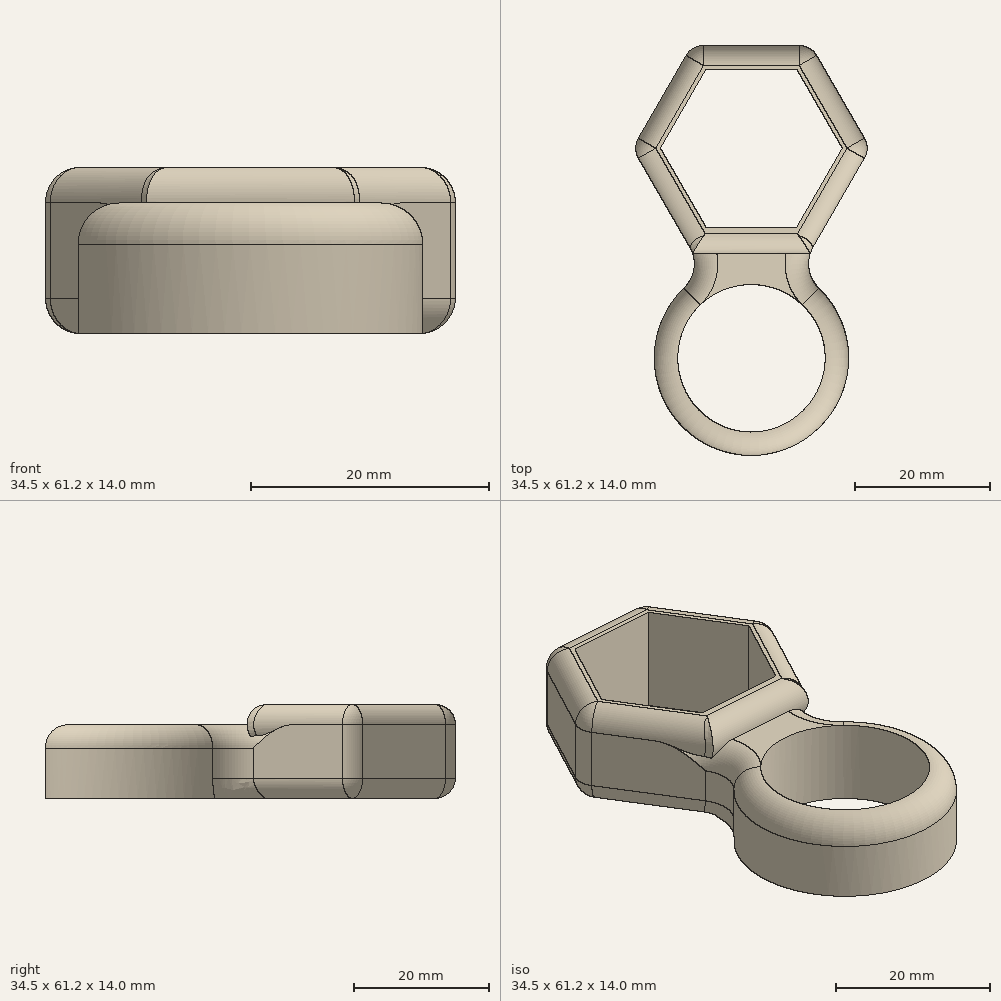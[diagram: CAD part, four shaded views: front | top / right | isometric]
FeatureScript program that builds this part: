
annotation { "Feature Type Name" : "Feature", "Feature Type Description" : "" }
export const myFeature = defineFeature(function(context is Context, id is Id, definition is map)
    precondition{}
    {
        {
            var Q0;
            Q0=qCreatedBy(makeId("Top.planeOp"),FACE);
            var sketch = newSketch(context, id + "F0", { "sketchPlane" : qUnion([Q0])});
            skCircle(sketch, "E0", {"center": v(0, 0) * mm, "radius": 47.5 * mm, "construction": true});
            skLineSegment(sketch, "E1", {"start": v(0, 32) * mm, "end": v(0, 0) * mm, "construction": true});
            skLineSegment(sketch, "E2", {"start": v(0, 0) * mm, "end": v(-27.71, -16) * mm, "construction": true});
            skLineSegment(sketch, "E3", {"start": v(0, 0) * mm, "end": v(27.71, -16) * mm, "construction": true});
            skCircle(sketch, "E4", {"center": v(0, 0) * mm, "radius": 14.5 * mm});
            skCircle(sketch, "E5.cCircle", {"center": v(0, 31.32) * mm, "radius": 11.75 * mm, "construction": true});
            skLineSegment(sketch, "E5.0", {"start": v(13.57, 31.32) * mm, "end": v(6.78, 19.57) * mm});
            skLineSegment(sketch, "E5.1", {"start": v(6.78, 19.57) * mm, "end": v(-6.78, 19.57) * mm});
            skLineSegment(sketch, "E5.2", {"start": v(-6.78, 19.57) * mm, "end": v(-13.57, 31.32) * mm});
            skLineSegment(sketch, "E5.3", {"start": v(-13.57, 31.32) * mm, "end": v(-6.78, 43.07) * mm});
            skLineSegment(sketch, "E5.4", {"start": v(-6.78, 43.07) * mm, "end": v(6.78, 43.07) * mm});
            skLineSegment(sketch, "E5.5", {"start": v(6.78, 43.07) * mm, "end": v(13.57, 31.32) * mm});
            skPoint(sketch, "E5.0.midPoint", {"position": v(10.18, 25.44) * mm});
            skCircle(sketch, "E6.cCircle", {"center": v(0, 31.32) * mm, "radius": 15.35 * mm, "construction": true});
            skLineSegment(sketch, "E6.0", {"start": v(17.72, 31.32) * mm, "end": v(8.86, 15.97) * mm});
            skLineSegment(sketch, "E6.1", {"start": v(8.86, 15.97) * mm, "end": v(-8.86, 15.97) * mm});
            skLineSegment(sketch, "E6.2", {"start": v(-8.86, 15.97) * mm, "end": v(-17.72, 31.32) * mm});
            skLineSegment(sketch, "E6.3", {"start": v(-17.72, 31.32) * mm, "end": v(-8.86, 46.67) * mm});
            skLineSegment(sketch, "E6.4", {"start": v(-8.86, 46.67) * mm, "end": v(8.86, 46.67) * mm});
            skLineSegment(sketch, "E6.5", {"start": v(8.86, 46.67) * mm, "end": v(17.72, 31.32) * mm});
            skPoint(sketch, "E6.0.midPoint", {"position": v(13.3, 23.64) * mm});
            skLineSegment(sketch, "E7", {"start": v(-8.86, 15.97) * mm, "end": v(-6.98, 12.7) * mm});
            skLineSegment(sketch, "E8", {"start": v(8.86, 15.97) * mm, "end": v(6.98, 12.7) * mm});
            skSolve(sketch);
        }
        {
            var Q0;
            Q0=qCreatedBy(makeId("Top.planeOp"),FACE);
            var sketch = newSketch(context, id + "F1", { "sketchPlane" : qUnion([Q0])});
            skCircle(sketch, "E9", {"center": v(0, 0) * mm, "radius": 11 * mm});
            skSolve(sketch);
        }
        {
            var Q0;
            Q0=qSketchRegion(id+"F0",true);
            extrude(context, id + "F2", {"entities" : qUnion([Q0]), "endBound" : BoundingType.SYMMETRIC, "depth" : 14 * mm, "offsetDistance" : 25 * mm});
        }
        {
            var Q0;
            Q0=makeQuery(id+"F2.opExtrude","CAP_FACE",FACE,{"disambiguationData":[OSD([sQuery(id+"F0.wireOp",EDGE,"E4"),sQuery(id+"F0.wireOp",EDGE,"E5.0"),sQuery(id+"F0.wireOp",EDGE,"E5.1"),sQuery(id+"F0.wireOp",EDGE,"E5.2"),sQuery(id+"F0.wireOp",EDGE,"E5.3"),sQuery(id+"F0.wireOp",EDGE,"E5.4"),sQuery(id+"F0.wireOp",EDGE,"E5.5"),sQuery(id+"F0.wireOp",EDGE,"E6.0"),sQuery(id+"F0.wireOp",EDGE,"E6.2"),sQuery(id+"F0.wireOp",EDGE,"E6.3"),sQuery(id+"F0.wireOp",EDGE,"E6.4"),sQuery(id+"F0.wireOp",EDGE,"E6.5"),sQuery(id+"F0.wireOp",EDGE,"E7"),sQuery(id+"F0.wireOp",EDGE,"E8")])],"isStart":false});
            var sketch = newSketch(context, id + "F3", { "sketchPlane" : qUnion([Q0])});
            skCircle(sketch, "E10", {"center": v(9.7, -5.3) * mm, "radius": 1.46 * mm});
            skSolve(sketch);
        }
        {
            var Q0;
            Q0=qSketchRegion(id+"F3",true);
            extrude(context, id + "F4", {"entities" : qUnion([Q0]), "operationType" : NewBodyOperationType.ADD, "oppositeDirection" : true, "depth" : 1 * mm, "offsetDistance" : 25 * mm});
        }
        {
            var Q0;
            Q0=qSketchRegion(id+"F1",true);
            extrude(context, id + "F5", {"entities" : qUnion([Q0]), "operationType" : NewBodyOperationType.REMOVE, "endBound" : BoundingType.SYMMETRIC, "oppositeDirection" : true, "depth" : 25 * mm, "offsetDistance" : 25 * mm});
        }
        {
            var Q0;
            Q0=qCreatedBy(makeId("Top.planeOp"),FACE);
            cPlane(context, id + "F6", {"entities" : qUnion([Q0]), "cplaneType" : CPlaneType.OFFSET, "offset" : 4 * mm, "width" : 150 * mm, "height" : 150 * mm});
        }
        {
            var Q0;
            Q0=qCreatedBy(id+"F6.planeOp",FACE);
            var sketch = newSketch(context, id + "F7", { "sketchPlane" : qUnion([Q0])});
            skCircle(sketch, "E11.cCircle", {"center": v(0, 0) * mm, "radius": 15.57 * mm, "construction": true});
            skLineSegment(sketch, "E11.0", {"start": v(8.99, 15.57) * mm, "end": v(17.97, 0) * mm});
            skLineSegment(sketch, "E11.1", {"start": v(17.97, 0) * mm, "end": v(8.99, -15.57) * mm});
            skLineSegment(sketch, "E11.2", {"start": v(8.99, -15.57) * mm, "end": v(-8.99, -15.57) * mm});
            skLineSegment(sketch, "E11.3", {"start": v(-8.99, -15.57) * mm, "end": v(-17.97, 0) * mm});
            skLineSegment(sketch, "E11.4", {"start": v(-17.97, 0) * mm, "end": v(-8.99, 15.57) * mm});
            skLineSegment(sketch, "E11.5", {"start": v(-8.99, 15.57) * mm, "end": v(8.99, 15.57) * mm});
            skPoint(sketch, "E11.0.midPoint", {"position": v(13.48, 7.78) * mm});
            skSolve(sketch);
        }
        {
            var Q0;
            Q0=qSketchRegion(id+"F7",true);
            extrude(context, id + "F8", {"entities" : qUnion([Q0]), "operationType" : NewBodyOperationType.REMOVE, "depth" : 3.5 * mm, "offsetDistance" : 25 * mm});
        }
        {
            var Q0;
            Q0=makeQuery(id+"FCyTIovh0KCK1Vn_1.2.F2.opExtrude","SWEPT_FACE",FACE,{"disambiguationData":[OSD([sQuery(id+"F0.wireOp",EDGE,"E6.4")])]});
            var Q1;
            Q1=makeQuery(id+"FCyTIovh0KCK1Vn_1.2.F2.opExtrude","SWEPT_FACE",FACE,{"disambiguationData":[OSD([sQuery(id+"F0.wireOp",EDGE,"E6.3")])]});
            var Q2;
            Q2=makeQuery(id+"FCyTIovh0KCK1Vn_1.2.F2.opExtrude","SWEPT_FACE",FACE,{"disambiguationData":[OSD([sQuery(id+"F0.wireOp",EDGE,"E6.5")])]});
            var Q3;
            Q3=makeQuery(id+"F2.opExtrude","SWEPT_FACE",FACE,{"disambiguationData":[OSD([sQuery(id+"F0.wireOp",EDGE,"E6.5")])]});
            var Q4;
            Q4=makeQuery(id+"F2.opExtrude","SWEPT_FACE",FACE,{"disambiguationData":[OSD([sQuery(id+"F0.wireOp",EDGE,"E6.3")])]});
            var Q5;
            Q5=makeQuery(id+"F2.opExtrude","SWEPT_FACE",FACE,{"disambiguationData":[OSD([sQuery(id+"F0.wireOp",EDGE,"E6.4")])]});
            var Q6;
            Q6=makeQuery(id+"FCyTIovh0KCK1Vn_1.1.F2.opExtrude","SWEPT_FACE",FACE,{"disambiguationData":[OSD([sQuery(id+"F0.wireOp",EDGE,"E6.5")])]});
            var Q7;
            Q7=makeQuery(id+"FCyTIovh0KCK1Vn_1.1.F2.opExtrude","SWEPT_FACE",FACE,{"disambiguationData":[OSD([sQuery(id+"F0.wireOp",EDGE,"E6.4")])]});
            var Q8;
            Q8=makeQuery(id+"FCyTIovh0KCK1Vn_1.1.F2.opExtrude","SWEPT_FACE",FACE,{"disambiguationData":[OSD([sQuery(id+"F0.wireOp",EDGE,"E6.3")])]});
            var Q9;
            Q9=makeQuery(id+"FCyTIovh0KCK1Vn_1.1.F2.opExtrude","CAP_EDGE",EDGE,{"disambiguationData":[OSD([sQuery(id+"F0.wireOp",EDGE,"E6.2"),sQuery(id+"F0.wireOp",EDGE,"E7")])],"isStart":true});
            var Q10;
            Q10=makeQuery(id+"FCyTIovh0KCK1Vn_1.1.F2.opExtrude","CAP_EDGE",EDGE,{"disambiguationData":[OSD([sQuery(id+"F0.wireOp",EDGE,"E6.2"),sQuery(id+"F0.wireOp",EDGE,"E7")])],"isStart":false});
            var Q11;
            {var subQ0=sQuery(id+"F0.wireOp",EDGE,"E8");var subQ1=sQuery(id+"F0.wireOp",EDGE,"E7");var subQ2=sQuery(id+"F0.wireOp",EDGE,"E6.5");var subQ3=sQuery(id+"F0.wireOp",EDGE,"E6.4");var subQ4=sQuery(id+"F0.wireOp",EDGE,"E6.3");var subQ5=sQuery(id+"F0.wireOp",EDGE,"E6.2");var subQ6=sQuery(id+"F0.wireOp",EDGE,"E6.0");var subQ7=sQuery(id+"F0.wireOp",EDGE,"E5.5");var subQ8=sQuery(id+"F0.wireOp",EDGE,"E5.4");var subQ9=sQuery(id+"F0.wireOp",EDGE,"E5.3");var subQ10=sQuery(id+"F0.wireOp",EDGE,"E5.2");var subQ11=sQuery(id+"F0.wireOp",EDGE,"E5.1");var subQ12=sQuery(id+"F0.wireOp",EDGE,"E5.0");var subQ13=sQuery(id+"F0.wireOp",EDGE,"E4");Q11=makeQuery(id+"F8.boolean.opBoolean","INTERSECT",EDGE,{"derivedFrom":[makeQuery(id+"F4.boolean.opBoolean","MERGE",FACE,{"derivedFrom":[makeQuery(id+"F2.opExtrude","CAP_FACE",FACE,{"disambiguationData":[OSD([subQ13,subQ12,subQ11,subQ10,subQ9,subQ8,subQ7,subQ6,subQ5,subQ4,subQ3,subQ2,subQ1,subQ0])],"isStart":false}),makeQuery(id+"FCyTIovh0KCK1Vn_1.1.F2.opExtrude","CAP_FACE",FACE,{"disambiguationData":[OSD([subQ13,subQ12,subQ11,subQ10,subQ9,subQ8,subQ7,subQ6,subQ5,subQ4,subQ3,subQ2,subQ1,subQ0])],"isStart":false}),makeQuery(id+"FCyTIovh0KCK1Vn_1.2.F2.opExtrude","CAP_FACE",FACE,{"disambiguationData":[OSD([subQ13,subQ12,subQ11,subQ10,subQ9,subQ8,subQ7,subQ6,subQ5,subQ4,subQ3,subQ2,subQ1,subQ0])],"isStart":false})]}),makeQuery(id+"F8.opExtrude","SWEPT_FACE",FACE,{"disambiguationData":[OSD([sQuery(id+"F7.wireOp",EDGE,"E11.3")])]})]});}
            var Q12;
            Q12=makeQuery(id+"FCyTIovh0KCK1Vn_1.1.F2.opExtrude","CAP_EDGE",EDGE,{"disambiguationData":[OSD([sQuery(id+"F0.wireOp",EDGE,"E6.0"),sQuery(id+"F0.wireOp",EDGE,"E8")])],"isStart":false});
            var Q13;
            Q13=makeQuery(id+"FCyTIovh0KCK1Vn_1.1.F2.opExtrude","CAP_EDGE",EDGE,{"disambiguationData":[OSD([sQuery(id+"F0.wireOp",EDGE,"E6.0"),sQuery(id+"F0.wireOp",EDGE,"E8")])],"isStart":true});
            var Q14;
            {var subQ0=sQuery(id+"F0.wireOp",EDGE,"E8");var subQ1=sQuery(id+"F0.wireOp",EDGE,"E7");var subQ2=sQuery(id+"F0.wireOp",EDGE,"E6.5");var subQ3=sQuery(id+"F0.wireOp",EDGE,"E6.4");var subQ4=sQuery(id+"F0.wireOp",EDGE,"E6.3");var subQ5=sQuery(id+"F0.wireOp",EDGE,"E6.2");var subQ6=sQuery(id+"F0.wireOp",EDGE,"E6.0");var subQ7=sQuery(id+"F0.wireOp",EDGE,"E5.5");var subQ8=sQuery(id+"F0.wireOp",EDGE,"E5.4");var subQ9=sQuery(id+"F0.wireOp",EDGE,"E5.3");var subQ10=sQuery(id+"F0.wireOp",EDGE,"E5.2");var subQ11=sQuery(id+"F0.wireOp",EDGE,"E5.1");var subQ12=sQuery(id+"F0.wireOp",EDGE,"E5.0");var subQ13=sQuery(id+"F0.wireOp",EDGE,"E4");Q14=makeQuery(id+"Fe9b3TNG2FXQlZz_1.1.F8.boolean.opBoolean","INTERSECT",EDGE,{"derivedFrom":[makeQuery(id+"F4.boolean.opBoolean","MERGE",FACE,{"derivedFrom":[makeQuery(id+"F2.opExtrude","CAP_FACE",FACE,{"disambiguationData":[OSD([subQ13,subQ12,subQ11,subQ10,subQ9,subQ8,subQ7,subQ6,subQ5,subQ4,subQ3,subQ2,subQ1,subQ0])],"isStart":true}),makeQuery(id+"FCyTIovh0KCK1Vn_1.1.F2.opExtrude","CAP_FACE",FACE,{"disambiguationData":[OSD([subQ13,subQ12,subQ11,subQ10,subQ9,subQ8,subQ7,subQ6,subQ5,subQ4,subQ3,subQ2,subQ1,subQ0])],"isStart":true}),makeQuery(id+"FCyTIovh0KCK1Vn_1.2.F2.opExtrude","CAP_FACE",FACE,{"disambiguationData":[OSD([subQ13,subQ12,subQ11,subQ10,subQ9,subQ8,subQ7,subQ6,subQ5,subQ4,subQ3,subQ2,subQ1,subQ0])],"isStart":true})]}),makeQuery(id+"Fe9b3TNG2FXQlZz_1.1.F8.opExtrude","SWEPT_FACE",FACE,{"disambiguationData":[OSD([sQuery(id+"F7.wireOp",EDGE,"E11.3")])]})]});}
            var Q15;
            Q15=makeQuery(id+"FCyTIovh0KCK1Vn_1.2.F2.opExtrude","CAP_EDGE",EDGE,{"disambiguationData":[OSD([sQuery(id+"F0.wireOp",EDGE,"E6.0"),sQuery(id+"F0.wireOp",EDGE,"E8")])],"isStart":true});
            var Q16;
            {var subQ0=sQuery(id+"F0.wireOp",EDGE,"E8");var subQ1=sQuery(id+"F0.wireOp",EDGE,"E7");var subQ2=sQuery(id+"F0.wireOp",EDGE,"E6.5");var subQ3=sQuery(id+"F0.wireOp",EDGE,"E6.4");var subQ4=sQuery(id+"F0.wireOp",EDGE,"E6.3");var subQ5=sQuery(id+"F0.wireOp",EDGE,"E6.2");var subQ6=sQuery(id+"F0.wireOp",EDGE,"E6.0");var subQ7=sQuery(id+"F0.wireOp",EDGE,"E5.5");var subQ8=sQuery(id+"F0.wireOp",EDGE,"E5.4");var subQ9=sQuery(id+"F0.wireOp",EDGE,"E5.3");var subQ10=sQuery(id+"F0.wireOp",EDGE,"E5.2");var subQ11=sQuery(id+"F0.wireOp",EDGE,"E5.1");var subQ12=sQuery(id+"F0.wireOp",EDGE,"E5.0");var subQ13=sQuery(id+"F0.wireOp",EDGE,"E4");Q16=makeQuery(id+"Fe9b3TNG2FXQlZz_1.1.F8.boolean.opBoolean","INTERSECT",EDGE,{"derivedFrom":[makeQuery(id+"F4.boolean.opBoolean","MERGE",FACE,{"derivedFrom":[makeQuery(id+"F2.opExtrude","CAP_FACE",FACE,{"disambiguationData":[OSD([subQ13,subQ12,subQ11,subQ10,subQ9,subQ8,subQ7,subQ6,subQ5,subQ4,subQ3,subQ2,subQ1,subQ0])],"isStart":true}),makeQuery(id+"FCyTIovh0KCK1Vn_1.1.F2.opExtrude","CAP_FACE",FACE,{"disambiguationData":[OSD([subQ13,subQ12,subQ11,subQ10,subQ9,subQ8,subQ7,subQ6,subQ5,subQ4,subQ3,subQ2,subQ1,subQ0])],"isStart":true}),makeQuery(id+"FCyTIovh0KCK1Vn_1.2.F2.opExtrude","CAP_FACE",FACE,{"disambiguationData":[OSD([subQ13,subQ12,subQ11,subQ10,subQ9,subQ8,subQ7,subQ6,subQ5,subQ4,subQ3,subQ2,subQ1,subQ0])],"isStart":true})]}),makeQuery(id+"Fe9b3TNG2FXQlZz_1.1.F8.opExtrude","SWEPT_FACE",FACE,{"disambiguationData":[OSD([sQuery(id+"F7.wireOp",EDGE,"E11.5")])]})]});}
            var Q17;
            Q17=makeQuery(id+"F2.opExtrude","CAP_EDGE",EDGE,{"disambiguationData":[OSD([sQuery(id+"F0.wireOp",EDGE,"E6.0"),sQuery(id+"F0.wireOp",EDGE,"E8")])],"isStart":true});
            var Q18;
            Q18=makeQuery(id+"F2.opExtrude","CAP_EDGE",EDGE,{"disambiguationData":[OSD([sQuery(id+"F0.wireOp",EDGE,"E6.2"),sQuery(id+"F0.wireOp",EDGE,"E7")])],"isStart":true});
            var Q19;
            {var subQ0=sQuery(id+"F0.wireOp",EDGE,"E8");var subQ1=sQuery(id+"F0.wireOp",EDGE,"E7");var subQ2=sQuery(id+"F0.wireOp",EDGE,"E6.5");var subQ3=sQuery(id+"F0.wireOp",EDGE,"E6.4");var subQ4=sQuery(id+"F0.wireOp",EDGE,"E6.3");var subQ5=sQuery(id+"F0.wireOp",EDGE,"E6.2");var subQ6=sQuery(id+"F0.wireOp",EDGE,"E6.0");var subQ7=sQuery(id+"F0.wireOp",EDGE,"E5.5");var subQ8=sQuery(id+"F0.wireOp",EDGE,"E5.4");var subQ9=sQuery(id+"F0.wireOp",EDGE,"E5.3");var subQ10=sQuery(id+"F0.wireOp",EDGE,"E5.2");var subQ11=sQuery(id+"F0.wireOp",EDGE,"E5.1");var subQ12=sQuery(id+"F0.wireOp",EDGE,"E5.0");var subQ13=sQuery(id+"F0.wireOp",EDGE,"E4");Q19=makeQuery(id+"Fe9b3TNG2FXQlZz_1.1.F8.boolean.opBoolean","INTERSECT",EDGE,{"derivedFrom":[makeQuery(id+"F4.boolean.opBoolean","MERGE",FACE,{"derivedFrom":[makeQuery(id+"F2.opExtrude","CAP_FACE",FACE,{"disambiguationData":[OSD([subQ13,subQ12,subQ11,subQ10,subQ9,subQ8,subQ7,subQ6,subQ5,subQ4,subQ3,subQ2,subQ1,subQ0])],"isStart":true}),makeQuery(id+"FCyTIovh0KCK1Vn_1.1.F2.opExtrude","CAP_FACE",FACE,{"disambiguationData":[OSD([subQ13,subQ12,subQ11,subQ10,subQ9,subQ8,subQ7,subQ6,subQ5,subQ4,subQ3,subQ2,subQ1,subQ0])],"isStart":true}),makeQuery(id+"FCyTIovh0KCK1Vn_1.2.F2.opExtrude","CAP_FACE",FACE,{"disambiguationData":[OSD([subQ13,subQ12,subQ11,subQ10,subQ9,subQ8,subQ7,subQ6,subQ5,subQ4,subQ3,subQ2,subQ1,subQ0])],"isStart":true})]}),makeQuery(id+"Fe9b3TNG2FXQlZz_1.1.F8.opExtrude","SWEPT_FACE",FACE,{"disambiguationData":[OSD([sQuery(id+"F7.wireOp",EDGE,"E11.1")])]})]});}
            var Q20;
            Q20=makeQuery(id+"FCyTIovh0KCK1Vn_1.2.F2.opExtrude","CAP_EDGE",EDGE,{"disambiguationData":[OSD([sQuery(id+"F0.wireOp",EDGE,"E6.2"),sQuery(id+"F0.wireOp",EDGE,"E7")])],"isStart":true});
            var Q21;
            Q21=makeQuery(id+"FCyTIovh0KCK1Vn_1.2.F2.opExtrude","CAP_EDGE",EDGE,{"disambiguationData":[OSD([sQuery(id+"F0.wireOp",EDGE,"E6.0"),sQuery(id+"F0.wireOp",EDGE,"E8")])],"isStart":false});
            var Q22;
            Q22=makeQuery(id+"FCyTIovh0KCK1Vn_1.2.F2.opExtrude","CAP_EDGE",EDGE,{"disambiguationData":[OSD([sQuery(id+"F0.wireOp",EDGE,"E6.2"),sQuery(id+"F0.wireOp",EDGE,"E7")])],"isStart":false});
            var Q23;
            {var subQ0=sQuery(id+"F0.wireOp",EDGE,"E8");var subQ1=sQuery(id+"F0.wireOp",EDGE,"E7");var subQ2=sQuery(id+"F0.wireOp",EDGE,"E6.5");var subQ3=sQuery(id+"F0.wireOp",EDGE,"E6.4");var subQ4=sQuery(id+"F0.wireOp",EDGE,"E6.3");var subQ5=sQuery(id+"F0.wireOp",EDGE,"E6.2");var subQ6=sQuery(id+"F0.wireOp",EDGE,"E6.0");var subQ7=sQuery(id+"F0.wireOp",EDGE,"E5.5");var subQ8=sQuery(id+"F0.wireOp",EDGE,"E5.4");var subQ9=sQuery(id+"F0.wireOp",EDGE,"E5.3");var subQ10=sQuery(id+"F0.wireOp",EDGE,"E5.2");var subQ11=sQuery(id+"F0.wireOp",EDGE,"E5.1");var subQ12=sQuery(id+"F0.wireOp",EDGE,"E5.0");var subQ13=sQuery(id+"F0.wireOp",EDGE,"E4");Q23=makeQuery(id+"F8.boolean.opBoolean","INTERSECT",EDGE,{"derivedFrom":[makeQuery(id+"F4.boolean.opBoolean","MERGE",FACE,{"derivedFrom":[makeQuery(id+"F2.opExtrude","CAP_FACE",FACE,{"disambiguationData":[OSD([subQ13,subQ12,subQ11,subQ10,subQ9,subQ8,subQ7,subQ6,subQ5,subQ4,subQ3,subQ2,subQ1,subQ0])],"isStart":false}),makeQuery(id+"FCyTIovh0KCK1Vn_1.1.F2.opExtrude","CAP_FACE",FACE,{"disambiguationData":[OSD([subQ13,subQ12,subQ11,subQ10,subQ9,subQ8,subQ7,subQ6,subQ5,subQ4,subQ3,subQ2,subQ1,subQ0])],"isStart":false}),makeQuery(id+"FCyTIovh0KCK1Vn_1.2.F2.opExtrude","CAP_FACE",FACE,{"disambiguationData":[OSD([subQ13,subQ12,subQ11,subQ10,subQ9,subQ8,subQ7,subQ6,subQ5,subQ4,subQ3,subQ2,subQ1,subQ0])],"isStart":false})]}),makeQuery(id+"F8.opExtrude","SWEPT_FACE",FACE,{"disambiguationData":[OSD([sQuery(id+"F7.wireOp",EDGE,"E11.1")])]})]});}
            var Q24;
            Q24=makeQuery(id+"F2.opExtrude","CAP_EDGE",EDGE,{"disambiguationData":[OSD([sQuery(id+"F0.wireOp",EDGE,"E6.2"),sQuery(id+"F0.wireOp",EDGE,"E7")])],"isStart":false});
            var Q25;
            {var subQ0=sQuery(id+"F0.wireOp",EDGE,"E8");var subQ1=sQuery(id+"F0.wireOp",EDGE,"E7");var subQ2=sQuery(id+"F0.wireOp",EDGE,"E6.5");var subQ3=sQuery(id+"F0.wireOp",EDGE,"E6.4");var subQ4=sQuery(id+"F0.wireOp",EDGE,"E6.3");var subQ5=sQuery(id+"F0.wireOp",EDGE,"E6.2");var subQ6=sQuery(id+"F0.wireOp",EDGE,"E6.0");var subQ7=sQuery(id+"F0.wireOp",EDGE,"E5.5");var subQ8=sQuery(id+"F0.wireOp",EDGE,"E5.4");var subQ9=sQuery(id+"F0.wireOp",EDGE,"E5.3");var subQ10=sQuery(id+"F0.wireOp",EDGE,"E5.2");var subQ11=sQuery(id+"F0.wireOp",EDGE,"E5.1");var subQ12=sQuery(id+"F0.wireOp",EDGE,"E5.0");var subQ13=sQuery(id+"F0.wireOp",EDGE,"E4");Q25=makeQuery(id+"F8.boolean.opBoolean","INTERSECT",EDGE,{"derivedFrom":[makeQuery(id+"F4.boolean.opBoolean","MERGE",FACE,{"derivedFrom":[makeQuery(id+"F2.opExtrude","CAP_FACE",FACE,{"disambiguationData":[OSD([subQ13,subQ12,subQ11,subQ10,subQ9,subQ8,subQ7,subQ6,subQ5,subQ4,subQ3,subQ2,subQ1,subQ0])],"isStart":false}),makeQuery(id+"FCyTIovh0KCK1Vn_1.1.F2.opExtrude","CAP_FACE",FACE,{"disambiguationData":[OSD([subQ13,subQ12,subQ11,subQ10,subQ9,subQ8,subQ7,subQ6,subQ5,subQ4,subQ3,subQ2,subQ1,subQ0])],"isStart":false}),makeQuery(id+"FCyTIovh0KCK1Vn_1.2.F2.opExtrude","CAP_FACE",FACE,{"disambiguationData":[OSD([subQ13,subQ12,subQ11,subQ10,subQ9,subQ8,subQ7,subQ6,subQ5,subQ4,subQ3,subQ2,subQ1,subQ0])],"isStart":false})]}),makeQuery(id+"F8.opExtrude","SWEPT_FACE",FACE,{"disambiguationData":[OSD([sQuery(id+"F7.wireOp",EDGE,"E11.5")])]})]});}
            var Q26;
            Q26=makeQuery(id+"F2.opExtrude","CAP_EDGE",EDGE,{"disambiguationData":[OSD([sQuery(id+"F0.wireOp",EDGE,"E6.0"),sQuery(id+"F0.wireOp",EDGE,"E8")])],"isStart":false});
            fillet(context, id + "F9", {"entities" : qUnion([Q0, Q1, Q2, Q3, Q4, Q5, Q6, Q7, Q8, Q9, Q10, Q11, Q12, Q13, Q14, Q15, Q16, Q17, Q18, Q19, Q20, Q21, Q22, Q23, Q24, Q25, Q26]), "radius" : 3 * mm, "tangentPropagation" : true, "allowEdgeOverflow" : false});
        }
        {
            var Q0;
            Q0=makeQuery(id+"F2.opExtrude","SWEPT_EDGE",EDGE,{"disambiguationData":[OSD([sQuery(id+"F0.wireOp",EDGE,"E4"),sQuery(id+"F0.wireOp",EDGE,"E8")])]});
            var Q1;
            Q1=makeQuery(id+"FCyTIovh0KCK1Vn_1.1.F2.opExtrude","SWEPT_EDGE",EDGE,{"disambiguationData":[OSD([sQuery(id+"F0.wireOp",EDGE,"E4"),sQuery(id+"F0.wireOp",EDGE,"E7")])]});
            var Q2;
            Q2=makeQuery(id+"F2.opExtrude","SWEPT_EDGE",EDGE,{"disambiguationData":[OSD([sQuery(id+"F0.wireOp",EDGE,"E4"),sQuery(id+"F0.wireOp",EDGE,"E7")])]});
            var Q3;
            Q3=makeQuery(id+"FCyTIovh0KCK1Vn_1.1.F2.opExtrude","SWEPT_EDGE",EDGE,{"disambiguationData":[OSD([sQuery(id+"F0.wireOp",EDGE,"E4"),sQuery(id+"F0.wireOp",EDGE,"E8")])]});
            fillet(context, id + "F10", {"entities" : qUnion([Q0, Q1, Q2, Q3]), "radius" : 5 * mm, "tangentPropagation" : true, "allowEdgeOverflow" : false});
        }
        {
            var Q0;
            {var subQ0=sQuery(id+"F0.wireOp",EDGE,"E8");var subQ1=sQuery(id+"F0.wireOp",EDGE,"E6.0");var subQ13=sQuery(id+"F0.wireOp",EDGE,"E4");Q0=makeQuery(id+"Fe9b3TNG2FXQlZz_1.1.F8.boolean.opBoolean","INTERSECT",EDGE,{"derivedFrom":[makeQuery(id+"F4.boolean.opBoolean","SPLIT",FACE,{"disambiguationData":[TD([makeQuery(id+"F2.opExtrude","SWEPT_FACE",FACE,{"disambiguationData":[OSD([subQ1,subQ0])]})])],"derivedFrom":makeQuery(id+"F2.opExtrude","SWEPT_FACE",FACE,{"disambiguationData":[OSD([subQ13])]})}),makeQuery(id+"Fe9b3TNG2FXQlZz_1.1.F8.opExtrude","CAP_FACE",FACE,{"disambiguationData":[OSD([sQuery(id+"F7.wireOp",EDGE,"E11.0"),sQuery(id+"F7.wireOp",EDGE,"E11.1"),sQuery(id+"F7.wireOp",EDGE,"E11.2"),sQuery(id+"F7.wireOp",EDGE,"E11.3"),sQuery(id+"F7.wireOp",EDGE,"E11.4"),sQuery(id+"F7.wireOp",EDGE,"E11.5")])],"isStart":true})]});}
            var Q1;
            {var subQ0=sQuery(id+"F0.wireOp",EDGE,"E8");var subQ1=sQuery(id+"F0.wireOp",EDGE,"E6.0");var subQ13=sQuery(id+"F0.wireOp",EDGE,"E4");Q1=makeQuery(id+"F8.boolean.opBoolean","INTERSECT",EDGE,{"derivedFrom":[makeQuery(id+"F4.boolean.opBoolean","SPLIT",FACE,{"disambiguationData":[TD([makeQuery(id+"F2.opExtrude","SWEPT_FACE",FACE,{"disambiguationData":[OSD([subQ1,subQ0])]})])],"derivedFrom":makeQuery(id+"F2.opExtrude","SWEPT_FACE",FACE,{"disambiguationData":[OSD([subQ13])]})}),makeQuery(id+"F8.opExtrude","CAP_FACE",FACE,{"disambiguationData":[OSD([sQuery(id+"F7.wireOp",EDGE,"E11.0"),sQuery(id+"F7.wireOp",EDGE,"E11.1"),sQuery(id+"F7.wireOp",EDGE,"E11.2"),sQuery(id+"F7.wireOp",EDGE,"E11.3"),sQuery(id+"F7.wireOp",EDGE,"E11.4"),sQuery(id+"F7.wireOp",EDGE,"E11.5")])],"isStart":true})]});}
            var Q2;
            {var subQ0=sQuery(id+"F0.wireOp",EDGE,"E7");var subQ1=sQuery(id+"F0.wireOp",EDGE,"E6.2");var subQ13=sQuery(id+"F0.wireOp",EDGE,"E4");Q2=makeQuery(id+"F8.boolean.opBoolean","INTERSECT",EDGE,{"derivedFrom":[makeQuery(id+"F4.boolean.opBoolean","SPLIT",FACE,{"disambiguationData":[TD([makeQuery(id+"F2.opExtrude","SWEPT_FACE",FACE,{"disambiguationData":[OSD([subQ1,subQ0])]})])],"derivedFrom":makeQuery(id+"F2.opExtrude","SWEPT_FACE",FACE,{"disambiguationData":[OSD([subQ13])]})}),makeQuery(id+"F8.opExtrude","CAP_FACE",FACE,{"disambiguationData":[OSD([sQuery(id+"F7.wireOp",EDGE,"E11.0"),sQuery(id+"F7.wireOp",EDGE,"E11.1"),sQuery(id+"F7.wireOp",EDGE,"E11.2"),sQuery(id+"F7.wireOp",EDGE,"E11.3"),sQuery(id+"F7.wireOp",EDGE,"E11.4"),sQuery(id+"F7.wireOp",EDGE,"E11.5")])],"isStart":true})]});}
            var Q3;
            {var subQ1=sQuery(id+"F0.wireOp",EDGE,"E7");var subQ5=sQuery(id+"F0.wireOp",EDGE,"E6.2");var subQ13=sQuery(id+"F0.wireOp",EDGE,"E4");Q3=makeQuery(id+"F8.boolean.opBoolean","INTERSECT",EDGE,{"derivedFrom":[makeQuery(id+"F4.boolean.opBoolean","SPLIT",FACE,{"disambiguationData":[TD([makeQuery(id+"FCyTIovh0KCK1Vn_1.1.F2.opExtrude","SWEPT_FACE",FACE,{"disambiguationData":[OSD([subQ5,subQ1])]})])],"derivedFrom":makeQuery(id+"F2.opExtrude","SWEPT_FACE",FACE,{"disambiguationData":[OSD([subQ13])]})}),makeQuery(id+"F8.opExtrude","CAP_FACE",FACE,{"disambiguationData":[OSD([sQuery(id+"F7.wireOp",EDGE,"E11.0"),sQuery(id+"F7.wireOp",EDGE,"E11.1"),sQuery(id+"F7.wireOp",EDGE,"E11.2"),sQuery(id+"F7.wireOp",EDGE,"E11.3"),sQuery(id+"F7.wireOp",EDGE,"E11.4"),sQuery(id+"F7.wireOp",EDGE,"E11.5")])],"isStart":true})]});}
            var Q4;
            {var subQ1=sQuery(id+"F0.wireOp",EDGE,"E7");var subQ5=sQuery(id+"F0.wireOp",EDGE,"E6.2");var subQ13=sQuery(id+"F0.wireOp",EDGE,"E4");Q4=makeQuery(id+"Fe9b3TNG2FXQlZz_1.1.F8.boolean.opBoolean","INTERSECT",EDGE,{"derivedFrom":[makeQuery(id+"F4.boolean.opBoolean","SPLIT",FACE,{"disambiguationData":[TD([makeQuery(id+"FCyTIovh0KCK1Vn_1.1.F2.opExtrude","SWEPT_FACE",FACE,{"disambiguationData":[OSD([subQ5,subQ1])]})])],"derivedFrom":makeQuery(id+"F2.opExtrude","SWEPT_FACE",FACE,{"disambiguationData":[OSD([subQ13])]})}),makeQuery(id+"Fe9b3TNG2FXQlZz_1.1.F8.opExtrude","CAP_FACE",FACE,{"disambiguationData":[OSD([sQuery(id+"F7.wireOp",EDGE,"E11.0"),sQuery(id+"F7.wireOp",EDGE,"E11.1"),sQuery(id+"F7.wireOp",EDGE,"E11.2"),sQuery(id+"F7.wireOp",EDGE,"E11.3"),sQuery(id+"F7.wireOp",EDGE,"E11.4"),sQuery(id+"F7.wireOp",EDGE,"E11.5")])],"isStart":true})]});}
            var Q5;
            {var subQ0=sQuery(id+"F0.wireOp",EDGE,"E7");var subQ1=sQuery(id+"F0.wireOp",EDGE,"E6.2");var subQ13=sQuery(id+"F0.wireOp",EDGE,"E4");Q5=makeQuery(id+"Fe9b3TNG2FXQlZz_1.1.F8.boolean.opBoolean","INTERSECT",EDGE,{"derivedFrom":[makeQuery(id+"F4.boolean.opBoolean","SPLIT",FACE,{"disambiguationData":[TD([makeQuery(id+"F2.opExtrude","SWEPT_FACE",FACE,{"disambiguationData":[OSD([subQ1,subQ0])]})])],"derivedFrom":makeQuery(id+"F2.opExtrude","SWEPT_FACE",FACE,{"disambiguationData":[OSD([subQ13])]})}),makeQuery(id+"Fe9b3TNG2FXQlZz_1.1.F8.opExtrude","CAP_FACE",FACE,{"disambiguationData":[OSD([sQuery(id+"F7.wireOp",EDGE,"E11.0"),sQuery(id+"F7.wireOp",EDGE,"E11.1"),sQuery(id+"F7.wireOp",EDGE,"E11.2"),sQuery(id+"F7.wireOp",EDGE,"E11.3"),sQuery(id+"F7.wireOp",EDGE,"E11.4"),sQuery(id+"F7.wireOp",EDGE,"E11.5")])],"isStart":true})]});}
            fillet(context, id + "F11", {"entities" : qUnion([Q0, Q1, Q2, Q3, Q4, Q5]), "radius" : 3.5 * mm, "tangentPropagation" : true, "allowEdgeOverflow" : false});
        }
    });
